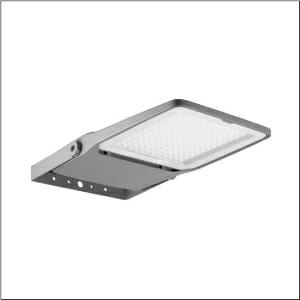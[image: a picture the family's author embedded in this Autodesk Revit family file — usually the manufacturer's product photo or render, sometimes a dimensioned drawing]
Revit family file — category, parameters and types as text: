
# Revit family: floodlight_fl_20_midi___pl43_5xa7682d2a2ac_b3e1
name_source: partatom
category: Lighting Fixtures
units: mm (PartAtom-declared; Revit-internal decimal feet)

## family parameters
Cut with Voids When Loaded = No
Host = Face
Light Source = No
Part Type = Normal
Room Calculation Point = No
Round Connector Dimension = Use Diameter
Shared = No

## types (1)
- --- (1 x LED 4000K / CRI = 70 (unbekannt), 19080 lm, 4000K)
    Apparent Load = 142 VA
    CIE Flux Codes = 32 74 99 100 100
    Color Rendering = 70
    Color Temperature = 4000K
    Default Elevation = 1800 mm
    Description = Floodlight FL 20 midi, floodlight, primary light control with lens, of plastic, primary optical cover: protective disc, of toughened safety glass, transparent, light distribution: PL43, light emission: direct distribution, primary light characteristic: asymmetric, installation type: surface-mounted, LED, High Power LED, rated luminous flux: 19.080lm, luminous efficacy: 134lm/W, light colour: 740, colour temperature: 4000K, control gear: ECG Plus, control: flexible luminous flux parameterisation, time-dependent luminous flux control, digital communication interface, power reduction, overheat protection, electronic power reduction, with terminal, 5-pole, max. 2.5mm², mains connection: 220..240V, AC, 50/60Hz, rated input power: 142W, LED unit, of diecast aluminium, powder-coated, Siteco® metallic grey (DB 702S), corrosivity category C5 mid according to DIN EN ISO 12944, incl. 1x M20 cable gland for cable Ø 6.5..12mm, length: 731mm, width: 450mm, height: 76mm, housing frame, of diecast aluminium, powder-coated, Siteco® metallic grey (DB 702S), wall fastening, of steel, powder-coated, Siteco® metallic grey (DB 702S), DALI, protection rating (complete): IP66, insulation class (complete): insulation class II (safety insulation), certification: CE, ENEC, VDE, protection symbol: D, permissible operating ambient temperature: -40..+40°C, permissible operating ambient temperature for outdoor applications: -40..+50°C, standard: DIN EN 12944, packaging unit: 1 piece

Light Distribution: PL43
    Height = 76 mm
    Lamp = 1 x LED 4000K / CRI >= 70 (unbekannt)
    Lamp Light Flux = 19080 lm
    Lamp count = 1
    Length = 731 mm
    Luminous efficacy = 134 lm/W
    Manufacturer = Siteco
    ModVariant = No
    Model = 5XA7682D2A2AC
    Mounting Place = Wall
    Mounting Type = Surface mounted
    Number of Poles = 1
    OnlyDefault = Yes
    Power Factor = 1
    Product Name = Floodlight FL 20 midi | PL43
    Product group = floodlight | wall mounted
    ProductGroupID = 2001
    Protection Class = Protection class II
    Protection Degree = IP 66
    RLX_Detail_Level = 1
    RLX_Emergency_Light_Flux = 0 lm
    RLX_Emergency_Type = 0
    RLX_Emergency_Type_DB = No
    RlxData = <blob elided: 91885 chars, md5=16ad0b8a>
    Socket = socket
    Standby Power = 0 W
    System Light Flux = 19080 lm
    System Power = 142 W
    Type Comments = factory setting: luminous flux: 100 % | dim-lin: 254 | 489 mA
    Type Image = l_1005944.jpg
    URL = http://relux.com
    VarID = @adj_148619
    Voltage = 0 V
    Weight = 0.00 kg
    Width = 450 mm

## geometry (parser evidence)
native form markers: Blend x4, Sweep x13
no freeform markers — native parametric forms only
